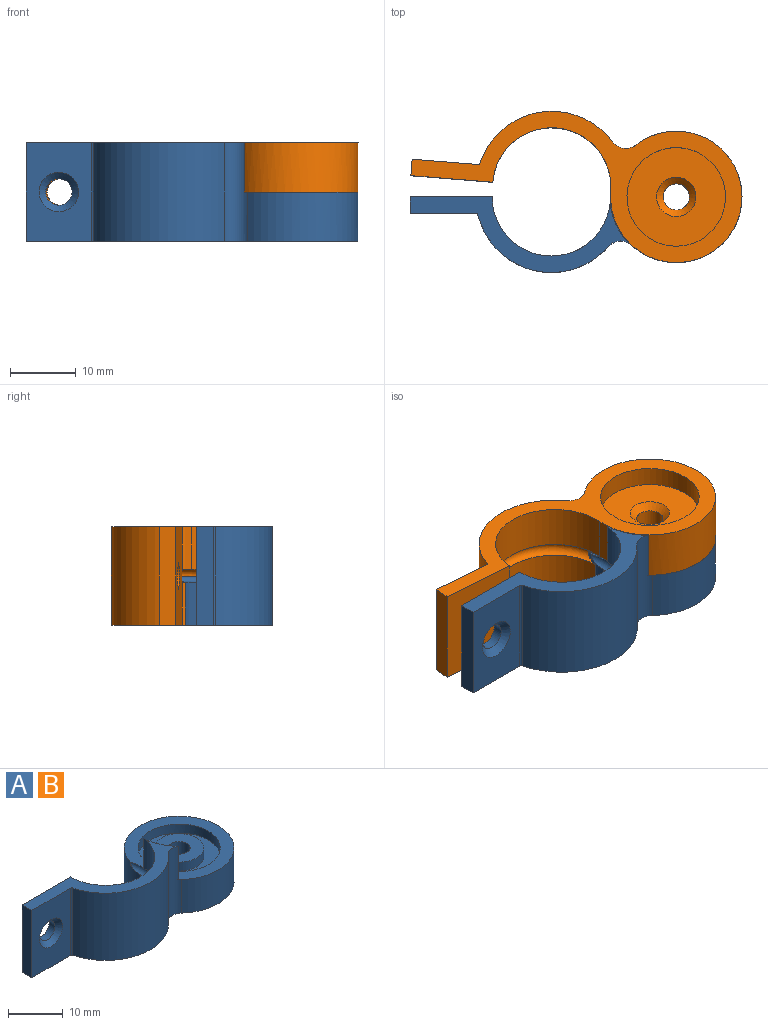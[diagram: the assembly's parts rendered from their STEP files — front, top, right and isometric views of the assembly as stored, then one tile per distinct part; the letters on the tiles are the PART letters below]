
ASSEMBLY  parts=2 mates=1
PART A: 26 faces, bbox 50.5x21.5x15 mm
  f0: plane 20x19.55mm, normal (0,0,1), area 136.7mm2, adj f3,f5,f7,f15,f23,f24,f25
  f1: plane 9x9mm, normal (0,0,1), area 51.1mm2, adj f8,f22
  f2: cylinder r=9mm len=17.95mm, axis (0,0,-1), area 177.4mm2, adj f4,f5,f10,f15
  f3: cylinder r=2.5mm len=15mm, axis (0,0,-1), area 55.1mm2, adj f0,f4,f7,f9,f14,f15
  f4: plane 33.22x11.5mm, normal (0,0,1), area 98.6mm2, adj f2,f3,f10,f11,f12,f13,f14,f15
  f5: torus R=9mm, axis (0,0,1), area 94.7mm2, adj f0,f2,f6,f7,f10,f15
  f6: cylinder r=9mm len=18mm, axis (0,0,-1), area 183.8mm2, adj f5,f7,f9,f10
  f7: cylinder r=10mm len=20mm, axis (0,0,-1), area 406.4mm2, adj f0,f3,f5,f6,f9
  f8: cylinder r=2mm len=4mm, axis (0,0,-1), area 44mm2, adj f1,f20
  f9: plane 50.5x21.5mm, normal (0,0,-1), area 236.8mm2, adj f3,f6,f7,f10,f11,f12,f13,f14
  f10: plane 15x12.5mm, normal (0,1,0), area 173.4mm2, adj f2,f4,f5,f6,f9,f11,f18
  f11: plane 15x2.5mm, normal (-1,0,0), area 37.5mm2, adj f4,f9,f10,f12
  f12: plane 15x10mm, normal (0,-1,0), area 121.7mm2, adj f4,f9,f11,f13,f19
  f13: cylinder r=0.35mm len=15mm, axis (0,0,-1), area 6.9mm2, adj f4,f9,f12,f14
  f14: cylinder r=11.5mm len=19.83mm, axis (0,0,-1), area 376.2mm2, adj f3,f4,f9,f13
  f15: cylinder r=10.1mm len=7.5mm, axis (0,0,-1), area 48.7mm2, adj f0,f2,f3,f4,f5
  f16: cylinder r=7.5mm len=15mm, axis (0,0,-1), area 141.4mm2, adj f9,f17
  f17: plane 15x15mm, normal (0,0,-1), area 148.4mm2, adj f16,f20
  f18: cylinder r=2mm len=4mm, axis (0,-1,0), area 18.8mm2, adj f10,f19
  f19: cone r=2mm half-angle=45deg, axis (0,-1,0), area 22.2mm2, adj f12,f18
  f20: cone r=3mm half-angle=45deg, axis (0,0,-1), area 22.2mm2, adj f8,f17
  f21: plane 15.41x15mm, normal (0,0,1), area 114.5mm2, adj f22,f23,f24,f25
  f22: cylinder r=4.5mm len=9mm, axis (0,0,-1), area 56.5mm2, adj f1,f21
  f23: cylinder r=5mm len=2.84mm, axis (0,0,-1), area 5.5mm2, adj f0,f21,f24,f25
  f24: torus R=9mm, axis (0,0,1), area 15.1mm2, adj f0,f21,f23,f25
  f25: cylinder r=7.5mm len=15mm, axis (0,0,-1), area 76.4mm2, adj f0,f21,f23,f24
PART B: same geometry as A
PLACE A t=(-4.21,2.92,-3.12)mm fixed
PLACE B rot(axis=(1,-0.04,0),180deg) t=(-4.15,4.44,11.88)mm
MATE revolute A.f8 <-> B.f8  axis (0,0,1) through (14.79,2.92,4.38)mm
